# Revit family: Basin-Countertop-American_Standard-Town_Square_S-1203_Series
name_source: partatom
category: Plumbing Fixtures
revit_build: Autodesk Revit 2014 (Build: 20130308_1515(x64)
units: mm (PartAtom-declared; Revit-internal decimal feet)

## types (3) — shared parameters
ADA Compliant = Yes
Assembly Code = D2010310
Basin Shape = Rectangle
CW Connection = Yes
CWFU = 1.5
Cold Water Connection Diameter = 1/2"
Cold Water Connection Height = 20 1/4"
Cold Water Connection Radius = 1/4"
Cold Water Connection Width = 4"
Default Elevation = 32 1/4"
Description = Town Square® S Countertop Sink
Finish = Vitreous China-American Standard-020-White
HW Connection = Yes
HWFU = 1.5
Height = 7 1/2"
Hot Water Connection Diameter = 1/2"
Hot Water Connection Height = 20 1/4"
Hot Water Connection Radius = 1/4"
Hot Water Connection Width = 4"
Installation Type = Countertop
Length = 19 1/16"
Manufacturer = American Standard
Material = Vitreous China-American Standard-020-White
Price = Prices may vary. Please consult Manufacturer Representative for most up-to-date price list.
URL = http://www.americanstandard-us.com
Vent Connection = No
WFU = 2
Waste Connection = Yes
Waste Connection Diameter = 1 1/4"
Waste Connection Height = 18 1/8"
Waste Connection Radius = 5/8"
Width = 24"

## per-type parameters (varying)
| type | Centerset Height | Centerset Holes | Hole Punch Location | Model |
| 1203004 | 9" | Yes | 2" | 1203004 |
| 1203008 | 9" | Yes | 4" | 0700.008.020 |
| 1203001 | 4" | No | 2" | 1203001 |

## geometry (parser evidence)
native form markers: Sweep x1
no freeform markers — native parametric forms only
